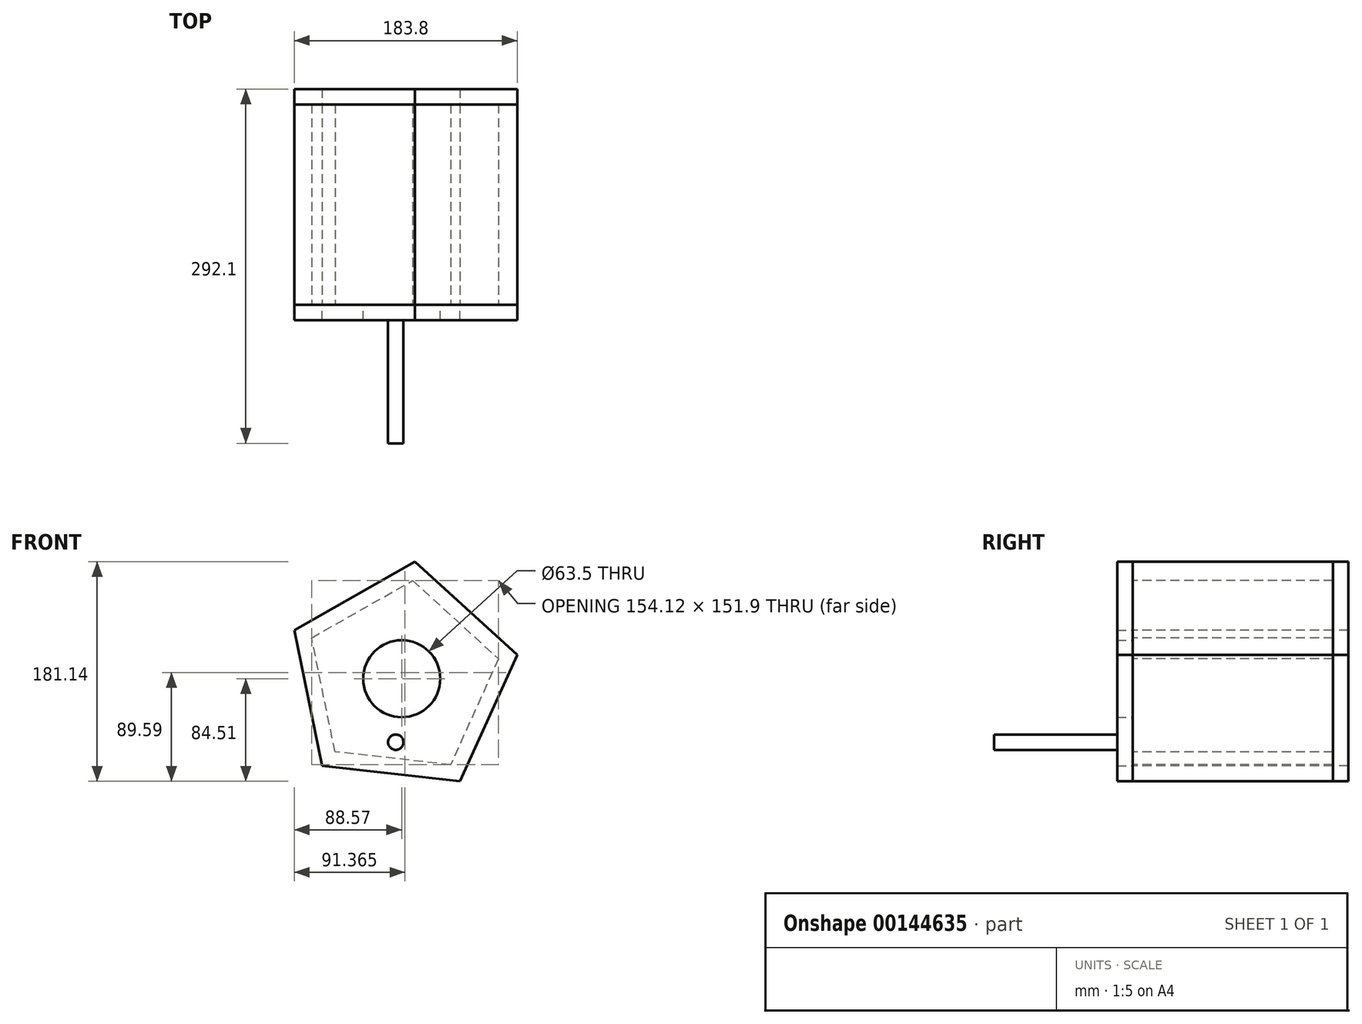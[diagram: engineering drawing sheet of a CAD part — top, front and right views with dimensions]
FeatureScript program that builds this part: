
annotation { "Feature Type Name" : "Feature", "Feature Type Description" : "" }
export const myFeature = defineFeature(function(context is Context, id is Id, definition is map)
    precondition{}
    {
        {
            var Q0;
            Q0=qCreatedBy(makeId("Front.planeOp"),FACE);
            var sketch = newSketch(context, id + "F0", { "sketchPlane" : qUnion([Q0])});
            skCircle(sketch, "E0.cCircle", {"center": v(0, 0) * mm, "radius": 78.66 * mm, "construction": true});
            skLineSegment(sketch, "E0.0", {"start": v(-88.57, 40.12) * mm, "end": v(10.78, 96.63) * mm});
            skLineSegment(sketch, "E0.1", {"start": v(10.78, 96.63) * mm, "end": v(95.23, 19.6) * mm});
            skLineSegment(sketch, "E0.2", {"start": v(95.23, 19.6) * mm, "end": v(48.07, -84.51) * mm});
            skLineSegment(sketch, "E0.3", {"start": v(48.07, -84.51) * mm, "end": v(-65.52, -71.84) * mm});
            skLineSegment(sketch, "E0.4", {"start": v(-65.52, -71.84) * mm, "end": v(-88.57, 40.12) * mm});
            skPoint(sketch, "E0.0.midPoint", {"position": v(-38.9, 68.37) * mm});
            skCircle(sketch, "E1", {"center": v(0, 0) * mm, "radius": 31.75 * mm});
            skLineSegment(sketch, "E2", {"start": v(10.78, 96.63) * mm, "end": v(-8.73, -78.17) * mm, "construction": true});
            skLineSegment(sketch, "E3", {"start": v(-88.57, 40.12) * mm, "end": v(95.23, 19.6) * mm, "construction": true});
            skSolve(sketch);
        }
        {
            var Q0;
            Q0 = qSketchRegion(id + "F0", true);
            extrude(context, id + "F1", {"entities" : qUnion([Q0]), "depth" : 12.7 * mm});
        }
        {
            var Q0;
            Q0=makeQuery(id+"F1.opExtrude","CAP_FACE",FACE,{"disambiguationData":[OSD([sQuery(id+"F0.wireOp",EDGE,"E0.0"),sQuery(id+"F0.wireOp",EDGE,"E0.1"),sQuery(id+"F0.wireOp",EDGE,"E0.2"),sQuery(id+"F0.wireOp",EDGE,"E0.3"),sQuery(id+"F0.wireOp",EDGE,"E0.4"),sQuery(id+"F0.wireOp",EDGE,"E1")])],"isStart":true});
            var sketch = newSketch(context, id + "F2", { "sketchPlane" : qUnion([Q0])});
            skLineSegment(sketch, "E4.0", {"start": v(-9.04, 81.03) * mm, "end": v(-79.86, 16.44) * mm});
            skLineSegment(sketch, "E5.0", {"start": v(-79.86, 16.44) * mm, "end": v(-40.31, -70.87) * mm});
            skLineSegment(sketch, "E6.0", {"start": v(-40.31, -70.87) * mm, "end": v(54.94, -60.24) * mm});
            skLineSegment(sketch, "E7.0", {"start": v(54.94, -60.24) * mm, "end": v(74.27, 33.64) * mm});
            skLineSegment(sketch, "E8.0", {"start": v(74.27, 33.64) * mm, "end": v(-9.04, 81.03) * mm});
            skLineSegment(sketch, "E9", {"start": v(-79.86, 16.44) * mm, "end": v(-9.04, 81.03) * mm});
            skLineSegment(sketch, "E10", {"start": v(-9.04, 81.03) * mm, "end": v(74.27, 33.64) * mm});
            skLineSegment(sketch, "E11", {"start": v(74.27, 33.64) * mm, "end": v(54.94, -60.24) * mm});
            skLineSegment(sketch, "E12", {"start": v(54.94, -60.24) * mm, "end": v(-40.31, -70.87) * mm});
            skLineSegment(sketch, "E13", {"start": v(-40.31, -70.87) * mm, "end": v(-79.86, 16.44) * mm});
            skLineSegment(sketch, "E14", {"start": v(-95.23, 19.6) * mm, "end": v(-10.78, 96.63) * mm});
            skLineSegment(sketch, "E15", {"start": v(-10.78, 96.63) * mm, "end": v(88.57, 40.12) * mm});
            skLineSegment(sketch, "E16", {"start": v(88.57, 40.12) * mm, "end": v(65.52, -71.84) * mm});
            skLineSegment(sketch, "E17", {"start": v(65.52, -71.84) * mm, "end": v(-48.07, -84.51) * mm});
            skLineSegment(sketch, "E18", {"start": v(-48.07, -84.51) * mm, "end": v(-95.23, 19.6) * mm});
            skSolve(sketch);
        }
        {
            var Q0;
            Q0 = qSketchRegion(id + "F2", true);
            extrude(context, id + "F3", {"entities" : qUnion([Q0]), "depth" : 165.1 * mm});
        }
        {
            var Q0;
            Q0=makeQuery(id+"F3.opExtrude","CAP_FACE",FACE,{"disambiguationData":[OSD([sQuery(id+"F2.wireOp",EDGE,"E9"),sQuery(id+"F2.wireOp",EDGE,"E10"),sQuery(id+"F2.wireOp",EDGE,"E11"),sQuery(id+"F2.wireOp",EDGE,"E12"),sQuery(id+"F2.wireOp",EDGE,"E13"),sQuery(id+"F2.wireOp",EDGE,"E14"),sQuery(id+"F2.wireOp",EDGE,"E15"),sQuery(id+"F2.wireOp",EDGE,"E16"),sQuery(id+"F2.wireOp",EDGE,"E17"),sQuery(id+"F2.wireOp",EDGE,"E18")])],"isStart":false});
            var sketch = newSketch(context, id + "F4", { "sketchPlane" : qUnion([Q0])});
            skLineSegment(sketch, "E19", {"start": v(-95.23, 19.6) * mm, "end": v(-48.07, -84.51) * mm});
            skLineSegment(sketch, "E20", {"start": v(-48.07, -84.51) * mm, "end": v(65.52, -71.84) * mm});
            skLineSegment(sketch, "E21", {"start": v(65.52, -71.84) * mm, "end": v(88.57, 40.12) * mm});
            skLineSegment(sketch, "E22", {"start": v(88.57, 40.12) * mm, "end": v(-10.78, 96.63) * mm});
            skLineSegment(sketch, "E23", {"start": v(-10.78, 96.63) * mm, "end": v(-95.23, 19.6) * mm});
            skSolve(sketch);
        }
        {
            var Q0;
            Q0 = qSketchRegion(id + "F4", true);
            extrude(context, id + "F5", {"entities" : qUnion([Q0]), "depth" : 12.7 * mm});
        }
        {
            var Q0;
            Q0=makeQuery(id+"F1.opExtrude","CAP_FACE",FACE,{"disambiguationData":[OSD([sQuery(id+"F0.wireOp",EDGE,"E0.0"),sQuery(id+"F0.wireOp",EDGE,"E0.1"),sQuery(id+"F0.wireOp",EDGE,"E0.2"),sQuery(id+"F0.wireOp",EDGE,"E0.3"),sQuery(id+"F0.wireOp",EDGE,"E0.4"),sQuery(id+"F0.wireOp",EDGE,"E1")])],"isStart":false});
            var sketch = newSketch(context, id + "F6", { "sketchPlane" : qUnion([Q0])});
            skCircle(sketch, "E24", {"center": v(-4.84, -52.32) * mm, "radius": 6.35 * mm});
            skSolve(sketch);
        }
        {
            var Q0;
            Q0 = qSketchRegion(id + "F6", true);
            extrude(context, id + "F7", {"entities" : qUnion([Q0]), "depth" : 101.6 * mm});
        }
    });
